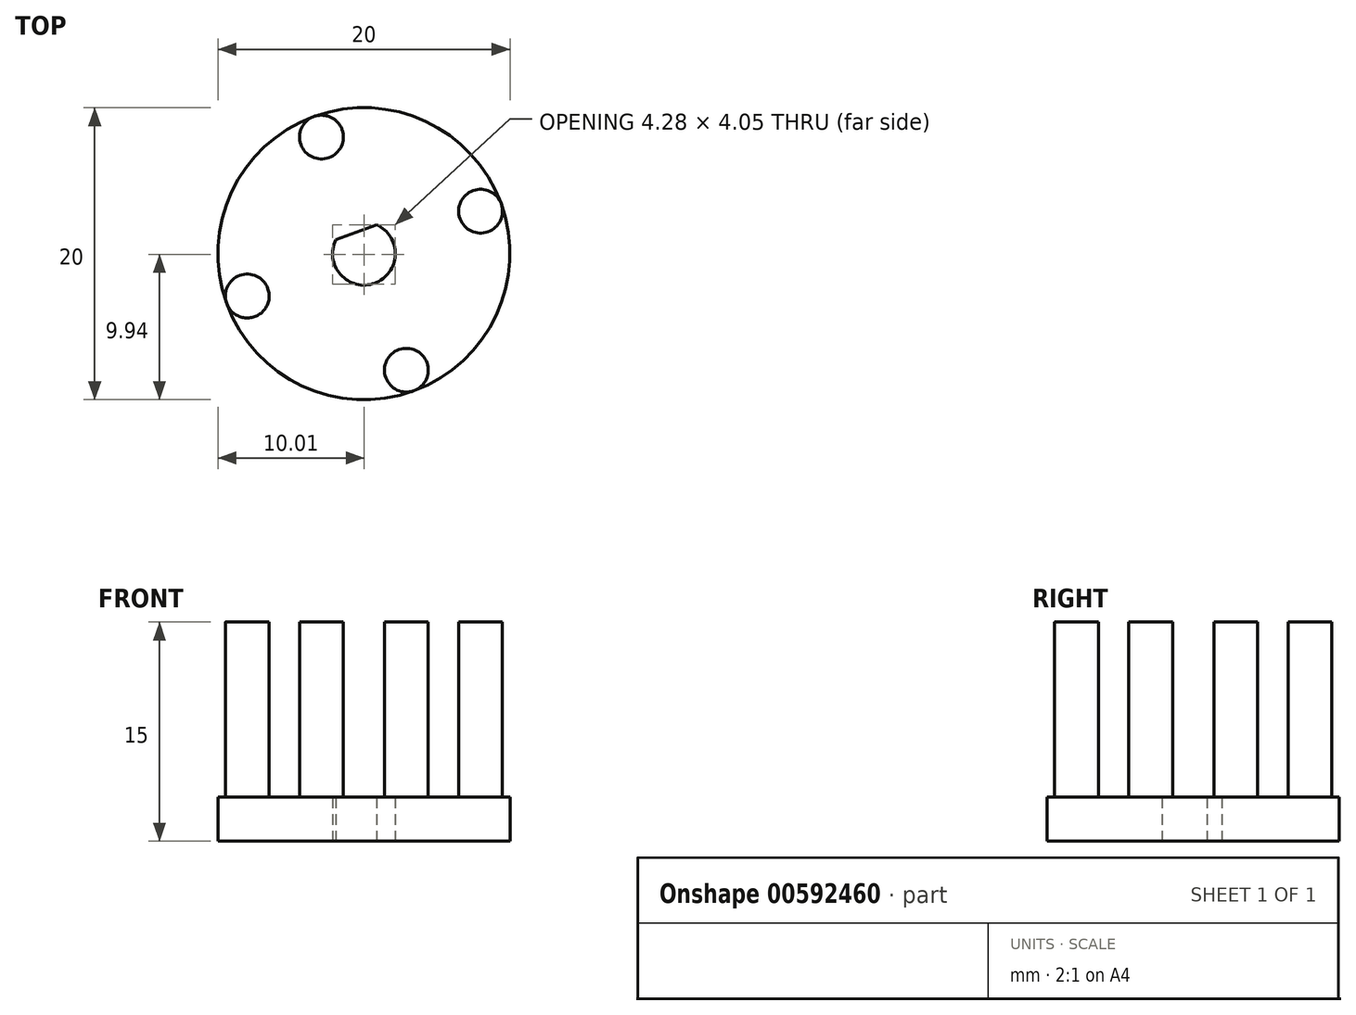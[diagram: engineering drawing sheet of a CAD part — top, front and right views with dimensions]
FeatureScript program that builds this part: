
annotation { "Feature Type Name" : "Feature", "Feature Type Description" : "" }
export const myFeature = defineFeature(function(context is Context, id is Id, definition is map)
    precondition{}
    {
        {
            var Q0;
            Q0=qCreatedBy(makeId("Top.planeOp"),FACE);
            var sketch = newSketch(context, id + "F0", { "sketchPlane" : qUnion([Q0])});
            skCircle(sketch, "E0", {"center": v(0, 0) * mm, "radius": 2.15 * mm});
            skLineSegment(sketch, "E1", {"start": v(-1.49, 1.55) * mm, "end": v(1.49, 1.55) * mm});
            skCircle(sketch, "E2", {"center": v(0, 0) * mm, "radius": 10 * mm});
            skCircle(sketch, "E3", {"center": v(0, 8.5) * mm, "radius": 1.5 * mm});
            skCircle(sketch, "E4.1.0", {"center": v(-8.5, 0) * mm, "radius": 1.5 * mm});
            skCircle(sketch, "E4.2.0", {"center": v(0, -8.5) * mm, "radius": 1.5 * mm});
            skCircle(sketch, "E4.3.0", {"center": v(8.5, 0) * mm, "radius": 1.5 * mm});
            skSolve(sketch);
        }
        {
            var Q0;
            {var subQ1=sQuery(id+"F0.wireOp",EDGE,"E3");Q0=makeQuery(id+"F0.imprint","IMPRINT",FACE,{"disambiguationData":[TD([[makeQuery(id+"F0.imprint","IMPRINT",EDGE,{"derivedFrom":subQ1}),-1.0]])]});}
            var Q1;
            Q1=makeQuery(id+"F0.imprint","IMPRINT",FACE,{"disambiguationData":[TD([[makeQuery(id+"F0.imprint","IMPRINT",EDGE,{"derivedFrom":sQuery(id+"F0.wireOp",EDGE,"E4.1.0")}),1.0]])]});
            var Q2;
            Q2=makeQuery(id+"F0.imprint","IMPRINT",FACE,{"disambiguationData":[TD([[makeQuery(id+"F0.imprint","IMPRINT",EDGE,{"derivedFrom":sQuery(id+"F0.wireOp",EDGE,"E4.2.0")}),1.0]])]});
            var Q3;
            Q3=makeQuery(id+"F0.imprint","IMPRINT",FACE,{"disambiguationData":[TD([[makeQuery(id+"F0.imprint","IMPRINT",EDGE,{"derivedFrom":sQuery(id+"F0.wireOp",EDGE,"E4.3.0")}),1.0]])]});
            var Q4;
            Q4=makeQuery(id+"F0.imprint","IMPRINT",FACE,{"disambiguationData":[TD([[makeQuery(id+"F0.imprint","IMPRINT",EDGE,{"derivedFrom":sQuery(id+"F0.wireOp",EDGE,"E4.4.0")}),1.0]])]});
            var Q5;
            Q5=makeQuery(id+"F0.imprint","IMPRINT",FACE,{"disambiguationData":[TD([[makeQuery(id+"F0.imprint","IMPRINT",EDGE,{"derivedFrom":sQuery(id+"F0.wireOp",EDGE,"E3")}),1.0]])]});
            var Q6;
            Q6=makeQuery(id+"F0.imprint","IMPRINT",FACE,{"disambiguationData":[TD([[makeQuery(id+"F0.imprint","IMPRINT",EDGE,{"derivedFrom":sQuery(id+"F0.wireOp",EDGE,"E4.5.0")}),1.0]])]});
            var Q7;
            {var subQ0=sQuery(id+"F0.wireOp",EDGE,"E1");Q7=makeQuery(id+"F0.imprint","IMPRINT",FACE,{"disambiguationData":[TD([[makeQuery(id+"F0.imprint","IMPRINT",EDGE,{"derivedFrom":subQ0}),1.0]])]});}
            extrude(context, id + "F1", {"entities" : qUnion([Q0, Q1, Q2, Q3, Q4, Q5, Q6, Q7]), "depth" : 3 * mm, "offsetDistance" : 25 * mm});
        }
        {
            var Q0;
            Q0=makeQuery(id+"F0.imprint","IMPRINT",FACE,{"disambiguationData":[TD([[makeQuery(id+"F0.imprint","IMPRINT",EDGE,{"derivedFrom":sQuery(id+"F0.wireOp",EDGE,"E3")}),1.0]])]});
            var Q1;
            Q1=makeQuery(id+"F0.imprint","IMPRINT",FACE,{"disambiguationData":[TD([[makeQuery(id+"F0.imprint","IMPRINT",EDGE,{"derivedFrom":sQuery(id+"F0.wireOp",EDGE,"E4.1.0")}),1.0]])]});
            var Q2;
            Q2=makeQuery(id+"F0.imprint","IMPRINT",FACE,{"disambiguationData":[TD([[makeQuery(id+"F0.imprint","IMPRINT",EDGE,{"derivedFrom":sQuery(id+"F0.wireOp",EDGE,"E4.2.0")}),1.0]])]});
            var Q3;
            Q3=makeQuery(id+"F0.imprint","IMPRINT",FACE,{"disambiguationData":[TD([[makeQuery(id+"F0.imprint","IMPRINT",EDGE,{"derivedFrom":sQuery(id+"F0.wireOp",EDGE,"E4.3.0")}),1.0]])]});
            var Q4;
            Q4=makeQuery(id+"F0.imprint","IMPRINT",FACE,{"disambiguationData":[TD([[makeQuery(id+"F0.imprint","IMPRINT",EDGE,{"derivedFrom":sQuery(id+"F0.wireOp",EDGE,"E4.4.0")}),1.0]])]});
            var Q5;
            Q5=makeQuery(id+"F0.imprint","IMPRINT",FACE,{"disambiguationData":[TD([[makeQuery(id+"F0.imprint","IMPRINT",EDGE,{"derivedFrom":sQuery(id+"F0.wireOp",EDGE,"E4.5.0")}),1.0]])]});
            extrude(context, id + "F2", {"entities" : qUnion([Q0, Q1, Q2, Q3, Q4, Q5]), "operationType" : NewBodyOperationType.ADD, "depth" : 15 * mm, "offsetDistance" : 25 * mm});
        }
        {
            var Q0;
            Q0=qCreatedBy(makeId("Front.planeOp"),FACE);
            var sketch = newSketch(context, id + "F3", { "sketchPlane" : qUnion([Q0])});
            skLineSegment(sketch, "E5", {"start": v(0, 0) * mm, "end": v(0, 48.72) * mm});
            skSolve(sketch);
        }
        {
            var Q0;
            Q0=makeQuery(id+"F1.opExtrude","SWEPT_BODY",BODY,{"disambiguationData":[OSD([sQuery(id+"F0.wireOp",EDGE,"E0"),sQuery(id+"F0.wireOp",EDGE,"E1"),sQuery(id+"F0.wireOp",EDGE,"E2")])]});
            var Q1;
            Q1=sQuery(id+"F3.wireOp",EDGE,"E5");
            transform(context, id + "F4", {"entities" : qUnion([Q0]), "transformType" : TransformType.ROTATION, "transformAxis" : qUnion([Q1]), "angle" : 20 * degree, "makeCopy" : false});
        }
    });
